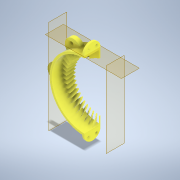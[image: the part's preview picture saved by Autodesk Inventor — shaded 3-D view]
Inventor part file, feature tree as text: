
AUTODESK INVENTOR PART (.ipt)
format: ipt  version: 2021.2 (Build 252289000, 289)  size: 1,256,960 bytes
history: native  units: in
note: dims shown in document units (in); Inventor stores cm internally (conversion verified against a paired STEP export)
features: extrude x10, sketch x10, plane x3, pattern_circular x3, fillet x2
ambient origin geometry x8: Origin, YZ Plane, XZ Plane, XY Plane, X Axis, Y Axis, Z Axis, Center Point
bodies: Solid1 (feature_tree)
feature tree (28):
  extrude  "Extrusion1"  Depth=4.25in
  plane  "Work Plane1"
  plane  "Work Plane2"
  extrude  "Extrusion3"  Depth=1.4in
  fillet  "Fillet1"  Radius=2.125in
  extrude  "Extrusion4"  TaperAngle=0.0deg  [1 undecoded]
  pattern_circular  "Circular Pattern2"  Count=2 Angle=360.0deg
  plane  "Work Plane3"
  extrude  "Extrusion5"  Depth=1.0in
  extrude  "Extrusion6"  Depth=0.5in
  fillet  "Fillet2"  [1 undecoded]
  extrude  "Extrusion7"  Depth=0.1in TaperAngle=0.0deg
  pattern_circular  "Circular Pattern3"  [2 undecoded]
  extrude  "Extrusion14"  Depth=0.5in
  pattern_circular  "Circular Pattern9"  [2 undecoded]
  extrude  "Extrusion15"  Depth=0.2in
  extrude  "Extrusion16"  Depth=0.5in TaperAngle=0.0deg
  extrude  "Extrusion17"  Depth=2.3622in TaperAngle=360.0deg
  sketch  "Sketch1"  dims[d0=4.0in d1=4.25in]
  sketch  "Sketch3"  dims[d2=1.0in d3=0.0in d4=1.4in d10=2.125in]
  sketch  "Sketch4"  dims[d11=0.25in d12=0.0in]
  sketch  "Sketch5"  dims[d13=0.5in d14=0.0in]
  sketch  "Sketch6"  dims[d15=0.5in]
  sketch  "Sketch7"  dims[d16=0.125in]
  sketch  "Sketch8"  dims[d17=0.2in]
  sketch  "Sketch11"  dims[d18=0.5in d19=0.0in d20=0.7874in d21=360.0deg]
  sketch  "Sketch12"  dims[d23=-2.125in d24=1.0in]
  sketch  "Sketch13"  dims[d25=0.25in d26=0.5in d27=0.0in d28=0.1in d29=0.0in d30=0.5in d31=0.0in d32=0.5in d33=0.25in d34=0.2in d35=0.5in d36=0.0in d37=2.3622in d38=360.0deg d40=0.25in d41=0.125in d42=0.25in d43=0.2in d49=0.5in d50=0.0312in d79=0.65in d80=0.0in d81=18.8976in d82=360.0deg d84=3.0625in d85=0.0in d86=0.0777in d87=0.0in d88=0.0in d89=0.8in d90=0.0in]
note: 6 required parameter values undecoded (feature->parameter linkage not recoverable at this tier; creation-order binding heuristic only, values carry confidence <= 0.55)
